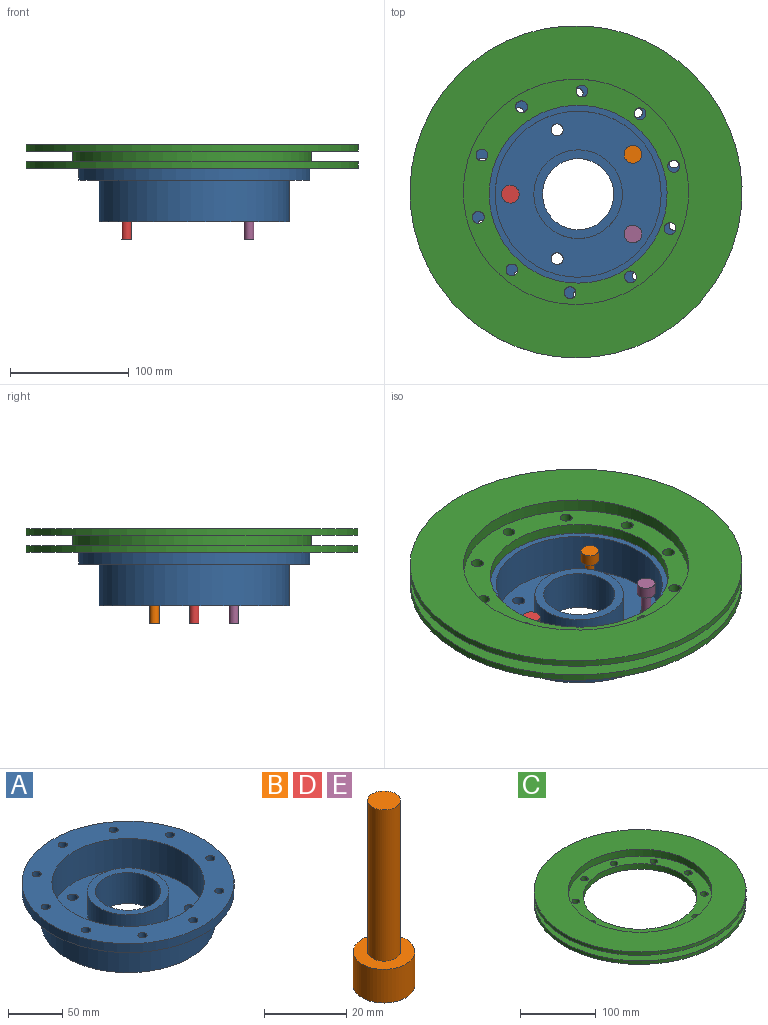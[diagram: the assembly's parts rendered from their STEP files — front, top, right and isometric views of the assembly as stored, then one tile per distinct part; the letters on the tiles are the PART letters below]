
ASSEMBLY  parts=5 mates=5
PART A: 25 faces, bbox 195x195x45 mm
  f0: cylinder r=5mm len=10mm, axis (0,0,-1), area 314.2mm2, adj f9,f21
  f1: cylinder r=5mm len=10mm, axis (0,0,-1), area 314.2mm2, adj f9,f21
  f2: cylinder r=5mm len=10mm, axis (0,0,-1), area 314.2mm2, adj f9,f21
  f3: cylinder r=5mm len=10mm, axis (0,0,-1), area 314.2mm2, adj f9,f21
  f4: cylinder r=5mm len=10mm, axis (0,0,-1), area 314.2mm2, adj f9,f21
  f5: cylinder r=30mm len=60mm, axis (0,0,-1), area 6597.3mm2, adj f9,f24
  f6: plane 195x195mm, normal (0,0,1), area 13923mm2, adj f10,f11,f12,f13,f14,f15,f16,f17
  f7: plane 195x195mm, normal (0,0,-1), area 9210.6mm2, adj f8,f10,f11,f12,f13,f14,f15,f16
  f8: cylinder r=80mm len=160mm, axis (0,0,-1), area 17592.9mm2, adj f7,f9
  f9: plane 160x160mm, normal (0,0,-1), area 16886.1mm2, adj f0,f1,f2,f3,f4,f5,f8
  f10: cylinder r=97.5mm len=195mm, axis (0,0,-1), area 6126.1mm2, adj f6,f7
  f11: cylinder r=4.18mm len=10mm, axis (0,0,-1), area 262.4mm2, adj f6,f7
  f12: cylinder r=4.18mm len=10mm, axis (0,0,-1), area 262.4mm2, adj f6,f7
  f13: cylinder r=4.18mm len=10mm, axis (0,0,-1), area 262.4mm2, adj f6,f7
  f14: cylinder r=4.18mm len=10mm, axis (0,0,-1), area 262.4mm2, adj f6,f7
  f15: cylinder r=4.18mm len=10mm, axis (0,0,-1), area 262.4mm2, adj f6,f7
  f16: cylinder r=4.18mm len=10mm, axis (0,0,-1), area 262.4mm2, adj f6,f7
  f17: cylinder r=4.18mm len=10mm, axis (0,0,-1), area 262.4mm2, adj f6,f7
  f18: cylinder r=4.18mm len=10mm, axis (0,0,-1), area 262.4mm2, adj f6,f7
  f19: cylinder r=4.18mm len=10mm, axis (0,0,-1), area 262.4mm2, adj f6,f7
  f20: cylinder r=4.18mm len=10mm, axis (0,0,-1), area 262.4mm2, adj f6,f7
  f21: plane 140x140mm, normal (0,0,1), area 10613.8mm2, adj f0,f1,f2,f3,f4,f22,f23
  f22: cylinder r=70mm len=140mm, axis (0,0,1), area 15393.8mm2, adj f6,f21
  f23: cylinder r=37.37mm len=74.74mm, axis (0,0,1), area 5870.1mm2, adj f21,f24
  f24: plane 74.74x74.74mm, normal (0,0,1), area 1559.9mm2, adj f5,f23
PART B: 5 faces, bbox 15x15x55 mm
  f0: cylinder r=7.5mm len=15mm, axis (0,0,-1), area 471.2mm2, adj f1,f2
  f1: plane 15x15mm, normal (0,0,1), area 126.4mm2, adj f0,f3
  f2: plane 15x15mm, normal (0,0,-1), area 176.7mm2, adj f0
  f3: cylinder r=4mm len=45mm, axis (0,0,-1), area 1131mm2, adj f1,f4
  f4: plane 8x8mm, normal (0,0,1), area 50.3mm2, adj f3
PART C: 20 faces, bbox 280x280x20 mm
  f0: cylinder r=5mm len=10mm, axis (0,0,-1), area 282.7mm2, adj f13,f17
  f1: cylinder r=5mm len=10mm, axis (0,0,-1), area 282.7mm2, adj f13,f17
  f2: cylinder r=5mm len=10mm, axis (0,0,-1), area 282.7mm2, adj f13,f17
  f3: cylinder r=5mm len=10mm, axis (0,0,-1), area 282.7mm2, adj f13,f17
  f4: cylinder r=5mm len=10mm, axis (0,0,-1), area 282.7mm2, adj f13,f17
  f5: cylinder r=5mm len=10mm, axis (0,0,-1), area 282.7mm2, adj f13,f17
  f6: cylinder r=5mm len=10mm, axis (0,0,-1), area 282.7mm2, adj f13,f17
  f7: cylinder r=5mm len=10mm, axis (0,0,-1), area 282.7mm2, adj f13,f17
  f8: cylinder r=5mm len=10mm, axis (0,0,-1), area 282.7mm2, adj f13,f17
  f9: cylinder r=140mm len=280mm, axis (0,0,-1), area 4838.1mm2, adj f13,f16
  f10: cylinder r=95mm len=190mm, axis (0,0,-1), area 6565.9mm2, adj f12,f17
  f11: cylinder r=140mm len=280mm, axis (0,0,-1), area 4838.1mm2, adj f12,f15
  f12: plane 280x280mm, normal (0,0,1), area 33222.3mm2, adj f10,f11
  f13: plane 280x280mm, normal (0,0,-1), area 43118.4mm2, adj f0,f1,f2,f3,f4,f5,f6,f7
  f14: cylinder r=100.5mm len=201mm, axis (0,0,-1), area 5683.1mm2, adj f15,f16
  f15: plane 280x280mm, normal (0,0,-1), area 29844.3mm2, adj f11,f14
  f16: plane 280x280mm, normal (0,0,1), area 29844.3mm2, adj f9,f14
  f17: plane 190x190mm, normal (0,0,1), area 9896mm2, adj f0,f1,f2,f3,f4,f5,f6,f7
  f18: cylinder r=75mm len=150mm, axis (0,0,-1), area 4241.2mm2, adj f13,f17
  f19: cylinder r=5mm len=10mm, axis (0,0,-1), area 282.7mm2, adj f13,f17
PART D: same geometry as B
PART E: same geometry as B
PLACE A t=(-14.68,-50.55,86.52)mm
PLACE B rot(axis=(1,0,0),180deg) t=(31.55,-16.96,126.52)mm
PLACE C rot(axis=(0,0,-1),90deg) t=(-16.49,-48.61,131.52)mm
PLACE D rot(axis=(1,0,0),180deg) t=(-71.83,-50.55,126.52)mm
PLACE E rot(axis=(1,0,0),180deg) t=(31.55,-84.14,126.52)mm
MATE planar D.f0 <-> E.f0  axis (0,0,1) through (-71.83,-50.55,126.52)mm
MATE planar C.f6 <-> A.f13  axis (0,0,-1) through (65.9,-27.1,131.52)mm
MATE cylindrical B.f3 <-> A.f2  axis (0,0,1) through (31.55,-16.96,94.02)mm
MATE planar E.f0 <-> B.f0  axis (0,0,1) through (31.55,-84.14,126.52)mm
MATE cylindrical C.f18 <-> A.f5  axis (0,0,-1) through (-14.68,-50.55,131.52)mm
